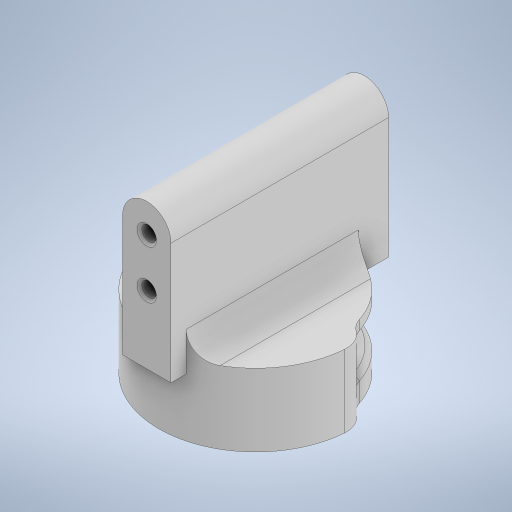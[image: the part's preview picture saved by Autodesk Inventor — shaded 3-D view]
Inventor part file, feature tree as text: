
AUTODESK INVENTOR PART (.ipt)
format: ipt  version: 2023.1 (Build 271208000, 208)  size: 366,080 bytes
history: native  units: mm
features: extrude x8, sketch x6, fillet x3, chamfer x2, other x1, projected_geometry x1
ambient origin geometry x8: Origin, YZ Plane, XZ Plane, XY Plane, X Axis, Y Axis, Z Axis, Center Point
bodies: Body1 (feature_tree)
feature tree (21):
  other  "솔리드1"
  extrude  "돌출1"  Depth=10.0mm
  extrude  "돌출2"  Depth=30.0mm
  fillet  "모깎기1"  Radius=45.0mm
  chamfer  "모따기1"  Distance=3.0mm
  sketch  "스케치3"
  extrude  "돌출3"  Depth=3.0mm
  extrude  "돌출5"  Depth=10.0mm
  extrude  "돌출6"  Depth=6.0mm
  fillet  "모깎기4"  Radius=30.0mm
  extrude  "돌출7"  Depth=5.0mm
  extrude  "돌출8"  Depth=0.5mm TaperAngle=45.0deg
  chamfer  "모따기2"  Distance=40.0mm
  fillet  "모깎기5"  Radius=2.0mm
  extrude  "돌출9"  Depth=3.0mm
  sketch  "스케치1"
  sketch  "스케치2"
  sketch  "스케치5"
  sketch  "스케치6"
  sketch  "스케치7"
  projected_geometry  "투영된 루프1"
